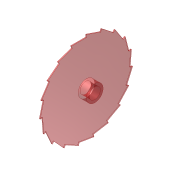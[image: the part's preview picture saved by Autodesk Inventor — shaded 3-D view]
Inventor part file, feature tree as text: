
AUTODESK INVENTOR PART (.ipt)
format: ipt  version: unknown  size: 222,208 bytes
history: native  units: in
note: dims shown in document units (in); Inventor stores cm internally (conversion verified against a paired STEP export)
features: sketch x3, extrude x2, revolve x1, plane x1, pattern_circular x1
ambient origin geometry x8: Origin, YZ Plane, XZ Plane, XY Plane, X Axis, Y Axis, Z Axis, Center Point
feature tree (8):
  revolve  "Revolution1"  [1 undecoded]
  sketch  "Sketch3"  dims[d5=90.0deg d26=0.1181in]
  plane  "Work Plane1"
  extrude  "Extrusion3"  Depth=0.1181in
  extrude  "Extrusion4"  Depth=0.0394in
  pattern_circular  "Circular Pattern3"  [2 undecoded]
  sketch  "Sketch1"  dims[d0=1.9685in d2=0.2756in d4=0.2362in]
  sketch  "Sketch4"  dims[d27=0.3937in d28=0.0394in d34=0.0079in d35=0.0787in d36=0.0in d37=0.0787in d38=0.0in d39=7.4803in d40=360.0deg]
note: 3 required parameter values undecoded (feature->parameter linkage not recoverable at this tier; creation-order binding heuristic only, values carry confidence <= 0.55)